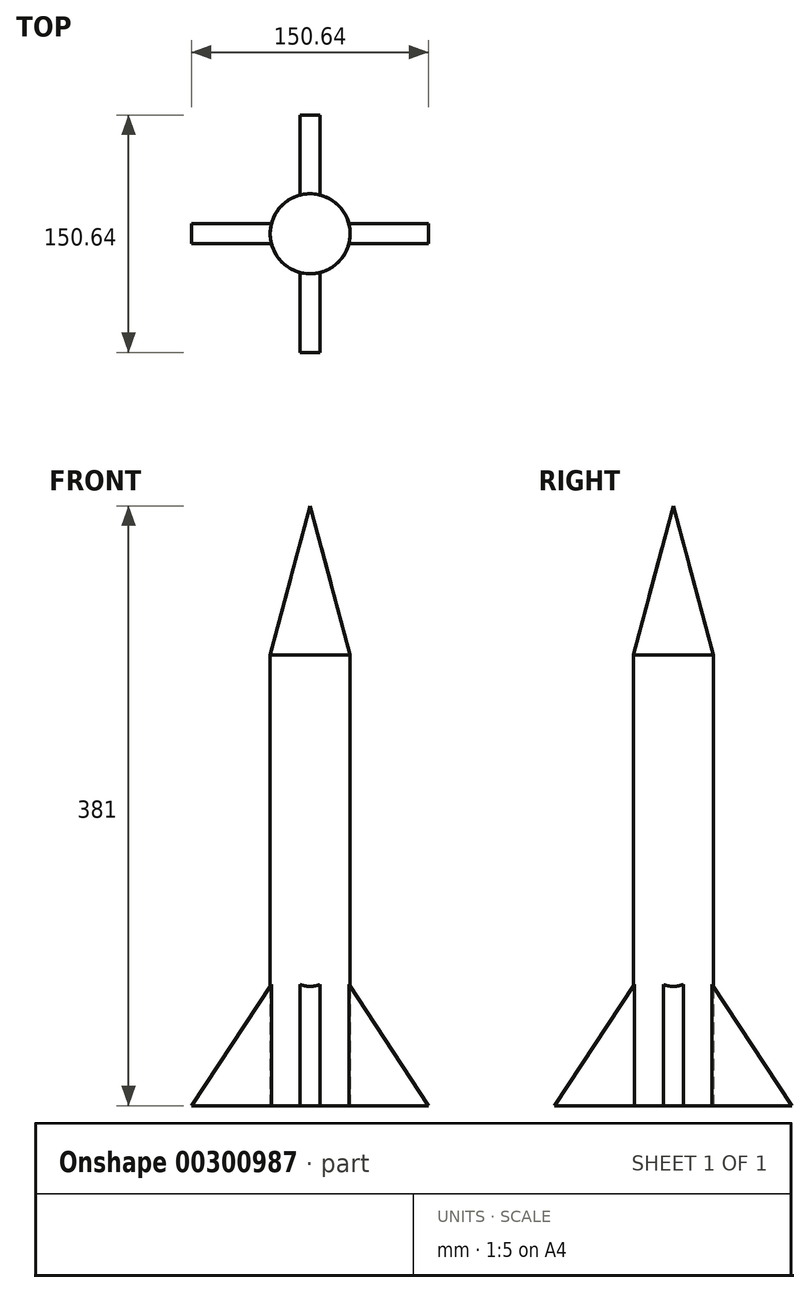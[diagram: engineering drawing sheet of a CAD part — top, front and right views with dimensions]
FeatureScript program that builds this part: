
annotation { "Feature Type Name" : "Feature", "Feature Type Description" : "" }
export const myFeature = defineFeature(function(context is Context, id is Id, definition is map)
    precondition{}
    {
        {
            var Q0;
            Q0=qCreatedBy(makeId("Top.planeOp"),FACE);
            var sketch = newSketch(context, id + "F0", { "sketchPlane" : qUnion([Q0])});
            skCircle(sketch, "E0", {"center": v(0, 0) * mm, "radius": 25.4 * mm});
            skSolve(sketch);
        }
        {
            var Q0;
            Q0 = qSketchRegion(id + "F0", true);
            extrude(context, id + "F1", {"entities" : qUnion([Q0]), "depth" : 381 * mm});
        }
        {
            var Q0;
            Q0=makeQuery(id+"F1.opExtrude","CAP_EDGE",EDGE,{"disambiguationData":[OSD([sQuery(id+"F0.wireOp",EDGE,"E0")])],"isStart":false});
            chamfer(context, id + "F2", {"entities" : qUnion([Q0]), "chamferType" : ChamferType.OFFSET_ANGLE, "width" : 25.4 * mm, "oppositeDirection" : false, "angle" : 75 * degree, "tangentPropagation" : true});
        }
        {
            var Q0;
            Q0=qCreatedBy(makeId("Front.planeOp"),FACE);
            var sketch = newSketch(context, id + "F3", { "sketchPlane" : qUnion([Q0])});
            skLineSegment(sketch, "E1", {"start": v(0, 0) * mm, "end": v(0, 114.35) * mm});
            skLineSegment(sketch, "E2", {"start": v(0, 114.35) * mm, "end": v(75.32, 0) * mm});
            skLineSegment(sketch, "E3", {"start": v(0, 0) * mm, "end": v(75.32, 0) * mm});
            skSolve(sketch);
        }
        {
            var Q0;
            Q0=makeQuery(id+"F3.imprint","IMPRINT",FACE,{"disambiguationData":[TD([[makeQuery(id+"F3.imprint","IMPRINT",EDGE,{"derivedFrom":sQuery(id+"F3.wireOp",EDGE,"E1")}),-1.0]])]});
            extrude(context, id + "F4", {"entities" : qUnion([Q0]), "operationType" : NewBodyOperationType.ADD, "endBound" : BoundingType.SYMMETRIC, "depth" : 12.7 * mm});
        }
        {
            var Q0;
            Q0=makeQuery(id+"F1.opExtrude","SWEPT_BODY",BODY,{"disambiguationData":[OSD([sQuery(id+"F0.wireOp",EDGE,"E0")])]});
            var Q1;
            Q1=makeQuery(id+"F1.opExtrude","SWEPT_FACE",FACE,{"disambiguationData":[OSD([sQuery(id+"F0.wireOp",EDGE,"E0")])]});
            circularPattern(context, id + "F5", {"entities" : qUnion([Q0]), "axis" : qUnion([Q1]), "angle" : 360 * degree, "instanceCount" : 4, "equalSpace" : true});
        }
    });
